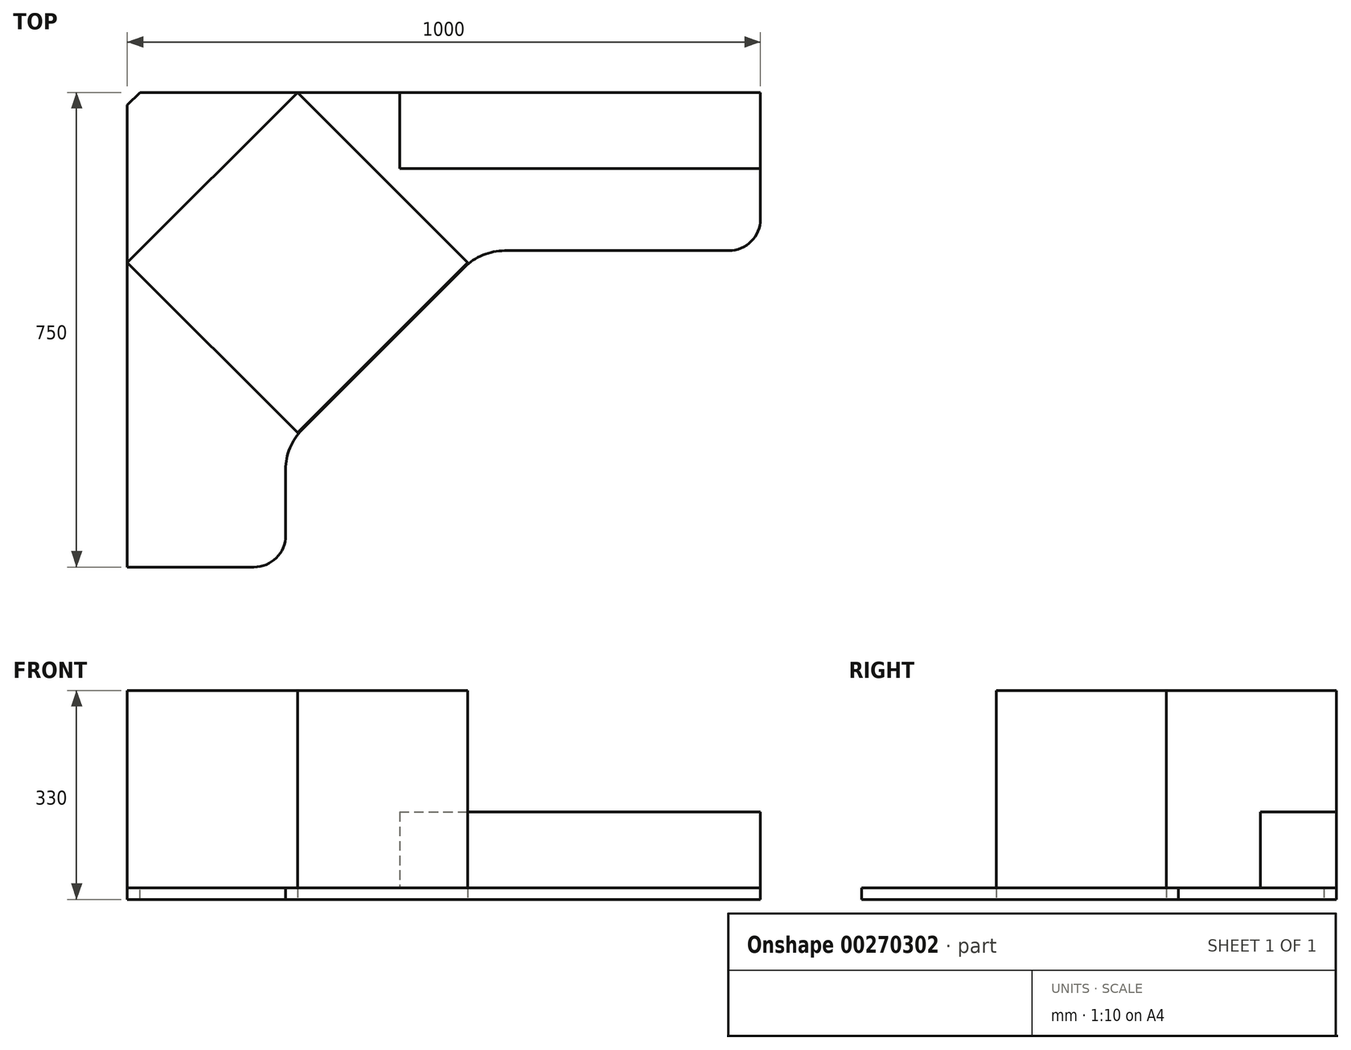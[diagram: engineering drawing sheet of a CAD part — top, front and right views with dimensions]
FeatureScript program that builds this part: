
annotation { "Feature Type Name" : "Feature", "Feature Type Description" : "" }
export const myFeature = defineFeature(function(context is Context, id is Id, definition is map)
    precondition{}
    {
        {
            var Q0;
            Q0=qCreatedBy(makeId("Top.planeOp"),FACE);
            var sketch = newSketch(context, id + "F0", { "sketchPlane" : qUnion([Q0])});
            skLineSegment(sketch, "E0", {"start": v(-702.45, 622.96) * mm, "end": v(297.55, 622.96) * mm});
            skLineSegment(sketch, "E1", {"start": v(-702.45, 622.96) * mm, "end": v(-702.45, -127.04) * mm});
            skLineSegment(sketch, "E2.0", {"start": v(-452.45, 26.93) * mm, "end": v(-452.45, -77.04) * mm});
            skLineSegment(sketch, "E3.0", {"start": v(-106.42, 372.96) * mm, "end": v(247.55, 372.96) * mm});
            skLineSegment(sketch, "E4", {"start": v(-702.45, -127.04) * mm, "end": v(-502.45, -127.04) * mm});
            skLineSegment(sketch, "E5", {"start": v(297.55, 622.96) * mm, "end": v(297.55, 422.96) * mm});
            skPoint(sketch, "E6.visualSharp", {"position": v(-452.45, -127.04) * mm});
            skArc(sketch, "E6.filletArc", {"start": v(-502.45, -127.04) * mm, "mid": v(-467.1, -112.4) * mm, "end": v(-452.45, -77.04) * mm});
            skPoint(sketch, "E7.visualSharp", {"position": v(-44.15, 330.9) * mm});
            skArc(sketch, "E7.filletArc", {"start": v(247.55, 372.96) * mm, "mid": v(282.9, 387.6) * mm, "end": v(297.55, 422.96) * mm});
            skLineSegment(sketch, "E8.right", {"start": v(-170.06, 346.6) * mm, "end": v(-426.1, 90.57) * mm});
            skArc(sketch, "E9", {"start": v(-426.1, 90.57) * mm, "mid": v(-445.6, 61.37) * mm, "end": v(-452.45, 26.93) * mm});
            skArc(sketch, "E10", {"start": v(-106.42, 372.96) * mm, "mid": v(-140.86, 366.11) * mm, "end": v(-170.06, 346.6) * mm});
            skSolve(sketch);
        }
        {
            var Q0;
            Q0 = qSketchRegion(id + "F0", true);
            extrude(context, id + "F1", {"entities" : qUnion([Q0]), "depth" : 18 * mm});
        }
        {
            var Q0;
            Q0=makeQuery(id+"F1.opExtrude","SWEPT_EDGE",EDGE,{"disambiguationData":[OSD([sQuery(id+"F0.wireOp",EDGE,"E0"),sQuery(id+"F0.wireOp",EDGE,"E1")])]});
            chamfer(context, id + "F2", {"entities" : qUnion([Q0]), "width" : 20 * mm, "tangentPropagation" : true});
        }
        {
            var Q0;
            Q0=qCreatedBy(makeId("Top.planeOp"),FACE);
            var sketch = newSketch(context, id + "F3", { "sketchPlane" : qUnion([Q0])});
            skLineSegment(sketch, "E11.bottom", {"start": v(-702.45, 354.26) * mm, "end": v(-433.75, 622.96) * mm});
            skLineSegment(sketch, "E11.top", {"start": v(-433.75, 85.56) * mm, "end": v(-165.05, 354.26) * mm});
            skLineSegment(sketch, "E11.left", {"start": v(-702.45, 354.26) * mm, "end": v(-433.75, 85.56) * mm});
            skLineSegment(sketch, "E11.right", {"start": v(-433.75, 622.96) * mm, "end": v(-165.05, 354.26) * mm});
            skSolve(sketch);
        }
        {
            var Q0;
            Q0 = qSketchRegion(id + "F3", true);
            extrude(context, id + "F4", {"entities" : qUnion([Q0]), "depth" : 330 * mm});
        }
        {
            var Q0;
            Q0 = qSketchRegion(id + "F3", true);
            extrude(context, id + "F5", {"entities" : qUnion([Q0]), "depth" : 330 * mm});
        }
        {
            var Q0;
            {var subQ0=sQuery(id+"F0.wireOp",EDGE,"E7.filletArc");var subQ1=sQuery(id+"F0.wireOp",EDGE,"E6.filletArc");var subQ2=sQuery(id+"F0.wireOp",EDGE,"E5");var subQ3=sQuery(id+"F0.wireOp",EDGE,"E4");var subQ4=sQuery(id+"F0.wireOp",EDGE,"E3.0");var subQ5=sQuery(id+"F0.wireOp",EDGE,"E0");var subQ6=sQuery(id+"F0.wireOp",EDGE,"E10");var subQ7=sQuery(id+"F0.wireOp",EDGE,"E9");var subQ8=sQuery(id+"F0.wireOp",EDGE,"E8.right");var subQ9=sQuery(id+"F0.wireOp",EDGE,"E2.0");var subQ10=sQuery(id+"F0.wireOp",EDGE,"E1");var subQ11=makeQuery(id+"F1.opExtrude","CAP_FACE",FACE,{"disambiguationData":[OSD([subQ5,subQ10,subQ9,subQ4,subQ3,subQ2,subQ1,subQ0,subQ8,subQ7,subQ6])],"isStart":false});Q0=makeQuery(id+"FN0LnI4H9hZN6qt_1.boolean.opBoolean","SPLIT",FACE,{"disambiguationData":[TD([makeQuery(id+"F1.opExtrude","SWEPT_FACE",FACE,{"disambiguationData":[OSD([subQ9])]})])],"derivedFrom":subQ11});}
            var sketch = newSketch(context, id + "F6", { "sketchPlane" : qUnion([Q0])});
            skLineSegment(sketch, "E12.bottom", {"start": v(-272.45, 622.96) * mm, "end": v(297.55, 622.96) * mm});
            skLineSegment(sketch, "E12.top", {"start": v(-272.45, 502.96) * mm, "end": v(297.55, 502.96) * mm});
            skLineSegment(sketch, "E12.left", {"start": v(-272.45, 622.96) * mm, "end": v(-272.45, 502.96) * mm});
            skLineSegment(sketch, "E12.right", {"start": v(297.55, 622.96) * mm, "end": v(297.55, 502.96) * mm});
            skSolve(sketch);
        }
        {
            var Q0;
            Q0 = qSketchRegion(id + "F6", true);
            extrude(context, id + "F7", {"entities" : qUnion([Q0]), "depth" : 120 * mm});
        }
    });
